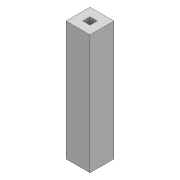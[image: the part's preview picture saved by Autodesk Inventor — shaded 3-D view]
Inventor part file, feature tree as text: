
AUTODESK INVENTOR PART (.ipt)
format: ipt  version: 2017 (Build 210142000, 142)  size: 85,504 bytes
history: native  units: mm
features: plane x1, extrude x1, sketch x1
ambient origin geometry x8: Origin, YZ Plane, XZ Plane, XY Plane, X Axis, Y Axis, Z Axis, Center Point
bodies: Body1 (feature_tree)
feature tree (3):
  plane  "Work Plane1"
  extrude  "Extrusion3"  Depth=9.0mm
  sketch  "Sketch2"  dims[d4=9.0mm d5=9.0mm d10=30.0mm d11=30.0mm d12=150.0mm d13=0.0mm]
